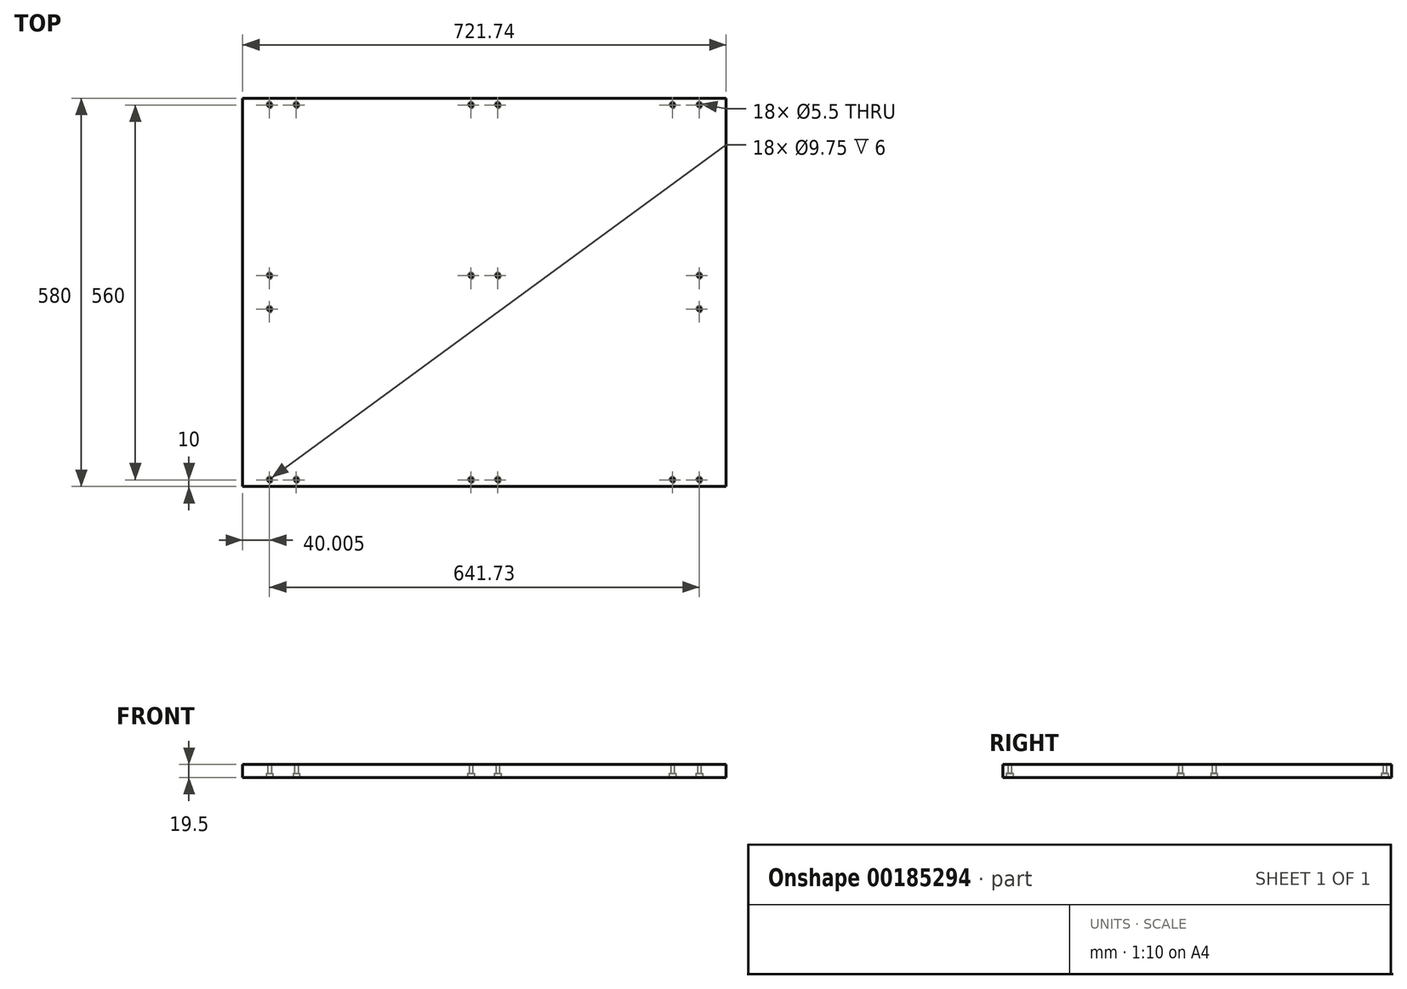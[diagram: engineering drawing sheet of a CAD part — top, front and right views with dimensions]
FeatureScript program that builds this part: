
annotation { "Feature Type Name" : "Feature", "Feature Type Description" : "" }
export const myFeature = defineFeature(function(context is Context, id is Id, definition is map)
    precondition{}
    {
        {
            var Q0;
            Q0=qCreatedBy(makeId("Top.planeOp"),FACE);
            var sketch = newSketch(context, id + "F0", { "sketchPlane" : qUnion([Q0])});
            skLineSegment(sketch, "E0.bottom", {"start": v(360.86, 290) * mm, "end": v(-360.87, 290) * mm});
            skLineSegment(sketch, "E0.top", {"start": v(360.87, -290) * mm, "end": v(-360.86, -290) * mm});
            skLineSegment(sketch, "E0.left", {"start": v(360.86, 290) * mm, "end": v(360.87, -290) * mm});
            skLineSegment(sketch, "E0.right", {"start": v(-360.87, 290) * mm, "end": v(-360.86, -290) * mm});
            skPoint(sketch, "E1", {"position": v(-320.87, 280) * mm});
            skPoint(sketch, "E2", {"position": v(-20, 280) * mm});
            skPoint(sketch, "E3", {"position": v(-20, -280) * mm});
            skPoint(sketch, "E4", {"position": v(-320.87, -280) * mm});
            skPoint(sketch, "E5", {"position": v(-320.87, 25) * mm});
            skPoint(sketch, "E6", {"position": v(20, 280) * mm});
            skPoint(sketch, "E7", {"position": v(320.86, 280) * mm});
            skPoint(sketch, "E8", {"position": v(-320.87, -25) * mm});
            skPoint(sketch, "E9", {"position": v(320.86, -25) * mm});
            skPoint(sketch, "E10", {"position": v(320.86, 25) * mm});
            skPoint(sketch, "E11", {"position": v(320.86, -280) * mm});
            skPoint(sketch, "E12", {"position": v(-20, 25) * mm});
            skPoint(sketch, "E13", {"position": v(20, 25) * mm});
            skPoint(sketch, "E14", {"position": v(20, -280) * mm});
            skPoint(sketch, "E15", {"position": v(-280.87, 280) * mm});
            skPoint(sketch, "E16", {"position": v(-280.87, -280) * mm});
            skPoint(sketch, "E17", {"position": v(280.86, -280) * mm});
            skPoint(sketch, "E18", {"position": v(280.86, 280) * mm});
            skSolve(sketch);
        }
        {
            var Q0;
            Q0 = qSketchRegion(id + "F0", true);
            extrude(context, id + "F1", {"entities" : qUnion([Q0]), "depth" : 19.5 * mm});
        }
        {
            var Q0;
            Q0=sQuery(id+"F0.wireOp",VERTEX,"E1");
            var Q1;
            Q1=sQuery(id+"F0.wireOp",VERTEX,"E2");
            var Q2;
            Q2=sQuery(id+"F0.wireOp",VERTEX,"E6");
            var Q3;
            Q3=sQuery(id+"F0.wireOp",VERTEX,"E7");
            var Q4;
            Q4=sQuery(id+"F0.wireOp",VERTEX,"E10");
            var Q5;
            Q5=sQuery(id+"F0.wireOp",VERTEX,"E9");
            var Q6;
            Q6=sQuery(id+"F0.wireOp",VERTEX,"E11");
            var Q7;
            Q7=sQuery(id+"F0.wireOp",VERTEX,"E14");
            var Q8;
            Q8=sQuery(id+"F0.wireOp",VERTEX,"E3");
            var Q9;
            Q9=sQuery(id+"F0.wireOp",VERTEX,"E4");
            var Q10;
            Q10=sQuery(id+"F0.wireOp",VERTEX,"E8");
            var Q11;
            Q11=sQuery(id+"F0.wireOp",VERTEX,"E5");
            var Q12;
            Q12=sQuery(id+"F0.wireOp",VERTEX,"E12");
            var Q13;
            Q13=sQuery(id+"F0.wireOp",VERTEX,"E13");
            var Q14;
            Q14=sQuery(id+"F0.wireOp",VERTEX,"E16");
            var Q15;
            Q15=sQuery(id+"F0.wireOp",VERTEX,"E15");
            var Q16;
            Q16=sQuery(id+"F0.wireOp",VERTEX,"E18");
            var Q17;
            Q17=sQuery(id+"F0.wireOp",VERTEX,"E17");
            var Q18;
            Q18=makeQuery(id+"F1.opExtrude","SWEPT_BODY",BODY,{"disambiguationData":[OSD([sQuery(id+"F0.wireOp",EDGE,"E0.bottom"),sQuery(id+"F0.wireOp",EDGE,"E0.top"),sQuery(id+"F0.wireOp",EDGE,"E0.left"),sQuery(id+"F0.wireOp",EDGE,"E0.right")])]});
            hole(context, id + "F2", {"style" : HoleStyle.C_BORE, "endStyle" : HoleEndStyle.THROUGH, "oppositeDirection" : true, "holeDiameter" : 5.5 * mm, "cBoreDiameter" : 9.75 * mm, "cBoreDepth" : 6 * mm, "locations" : qUnion([Q0, Q1, Q2, Q3, Q4, Q5, Q6, Q7, Q8, Q9, Q10, Q11, Q12, Q13, Q14, Q15, Q16, Q17]), "scope" : qUnion([Q18]), "isTappedThrough" : true});
        }
    });
